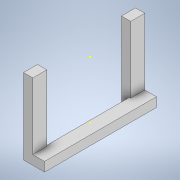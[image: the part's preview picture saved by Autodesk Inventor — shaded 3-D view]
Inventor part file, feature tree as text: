
AUTODESK INVENTOR PART (.ipt)
format: ipt  version: 2020 (Build 240168000, 168)  size: 146,432 bytes
history: native  units: mm
features: sketch x7, extrude x5
ambient origin geometry x8: Origin, YZ Plane, XZ Plane, XY Plane, X Axis, Y Axis, Z Axis, Center Point
bodies: Solid1 (feature_tree)
feature tree (12):
  extrude  "Extrusion1"  Depth=48.0mm
  extrude  "Extrusion2"  Depth=4.0mm
  sketch  "Sketch3"  dims[d5=6.0mm d6=4.0mm]
  extrude  "Extrusion3"  Depth=4.0mm
  extrude  "Extrusion4"  Depth=6.0mm TaperAngle=0.0deg
  sketch  "Sketch6"  dims[d12=4.0mm d13=0.0mm]
  extrude  "Extrusion5"  Depth=36.0mm
  sketch  "Sketch1"  dims[d0=9.0mm d1=48.0mm]
  sketch  "Sketch2"  dims[d2=4.0mm d3=0.0mm d4=4.0mm]
  sketch  "Sketch4"  dims[d7=6.0mm d8=24.5mm d9=0.0mm]
  sketch  "Sketch5"  dims[d10=5.5mm d11=36.0mm]
  sketch  "Sketch7"  dims[d14=36.0mm d15=4.0mm d16=2.0mm d17=0.0mm d18=4.0mm d19=0.0mm]
